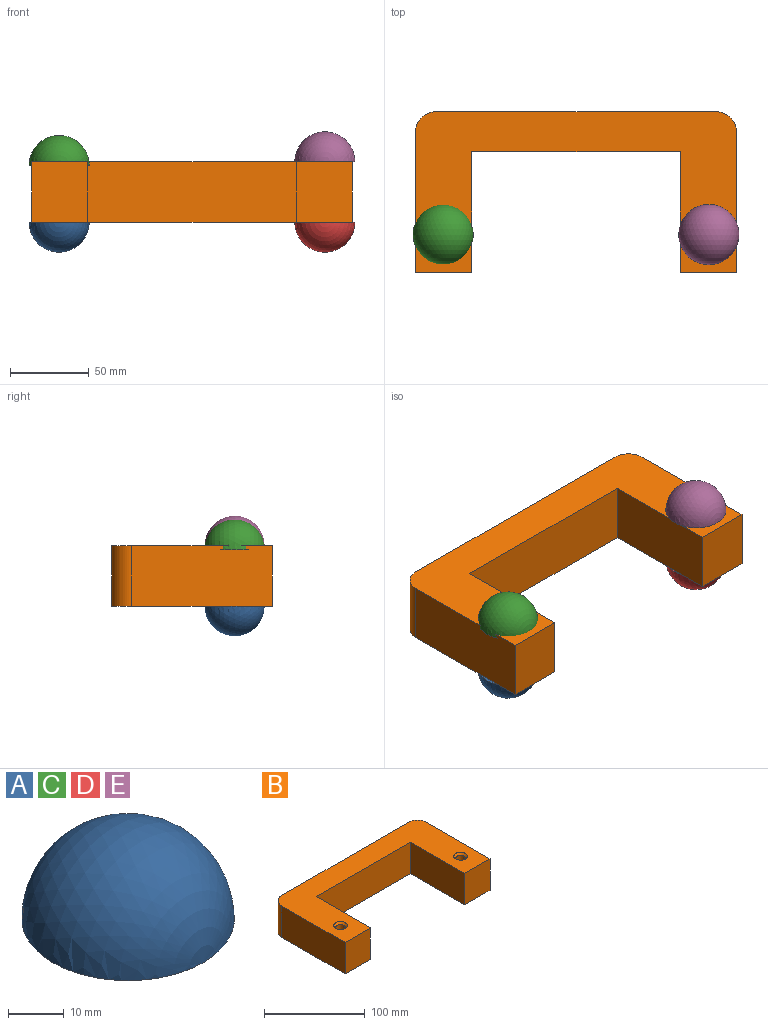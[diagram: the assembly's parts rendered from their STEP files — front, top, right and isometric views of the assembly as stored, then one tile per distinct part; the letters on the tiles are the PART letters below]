
ASSEMBLY  parts=5 mates=4
PART A: 2 faces, bbox 38.1x38.1x19.1 mm
  f0: sphere r=19.05mm, area 2280.2mm2, adj f1
  f1: plane 38.1x38.1mm, normal (0,0,-1), area 1140.1mm2, adj f0
PART B: 16 faces, bbox 203.2x101.6x38.1 mm
  f0: plane 88.9x38.1mm, normal (-1,0,0), area 3387.1mm2, adj f1,f9,f10,f11
  f1: plane 38.1x35.56mm, normal (0,-1,0), area 1354.8mm2, adj f0,f2,f10,f11
  f2: plane 76.2x38.1mm, normal (1,0,0), area 2903.2mm2, adj f1,f3,f10,f11
  f3: plane 132.08x38.1mm, normal (0,-1,0), area 5032.2mm2, adj f2,f4,f10,f11
  f4: plane 76.2x38.1mm, normal (-1,0,0), area 2903.2mm2, adj f3,f5,f10,f11
  f5: plane 38.1x35.56mm, normal (0,-1,0), area 1354.8mm2, adj f4,f6,f10,f11
  f6: plane 88.9x38.1mm, normal (1,0,0), area 3387.1mm2, adj f5,f7,f10,f11
  f7: cylinder r=12.7mm len=38.1mm, axis (0,0,-1), area 760.1mm2, adj f6,f8,f10,f11
  f8: plane 177.8x38.1mm, normal (0,1,0), area 6774.2mm2, adj f7,f9,f10,f11
  f9: cylinder r=12.7mm len=38.1mm, axis (0,0,-1), area 760.1mm2, adj f0,f8,f10,f11
  f10: plane 203.2x101.6mm, normal (0,0,1), area 10225.7mm2, adj f0,f1,f2,f3,f4,f5,f6,f7
  f11: plane 203.2x101.6mm, normal (0,0,-1), area 10368.9mm2, adj f0,f1,f2,f3,f4,f5,f6,f7
  f12: cylinder r=4.76mm len=35.82mm, axis (0,0,1), area 1071.9mm2, adj f11,f13
  f13: cone r=4.76mm half-angle=41deg, axis (0,0,1), area 109.2mm2, adj f10,f12
  f14: cylinder r=4.76mm len=35.82mm, axis (0,0,1), area 1071.9mm2, adj f11,f15
  f15: cone r=4.76mm half-angle=41deg, axis (0,0,1), area 109.2mm2, adj f10,f14
PART C: same geometry as A
PART D: same geometry as A
PART E: same geometry as A
PLACE A rot(axis=(1,0,0),180deg) t=(-72.95,-4.23,5.39)mm
PLACE B t=(2.56,14.82,5.39)mm fixed
PLACE C t=(-72.95,-4.23,41.21)mm
PLACE D rot(axis=(1,0,0),180deg) t=(95.33,-4.23,5.39)mm
PLACE E t=(95.33,-4.23,43.49)mm
MATE ball C.f1 <-> B.f12  axis (0,0,-1) through (-72.95,-4.23,41.21)mm
MATE ball A.f1 <-> B.f12  axis (0,0,1) through (-72.95,-4.23,5.39)mm
MATE ball E.f1 <-> B.f14  axis (0,0,-1) through (95.33,-4.23,43.49)mm
MATE ball D.f1 <-> B.f14  axis (0,0,1) through (95.33,-4.23,5.39)mm
